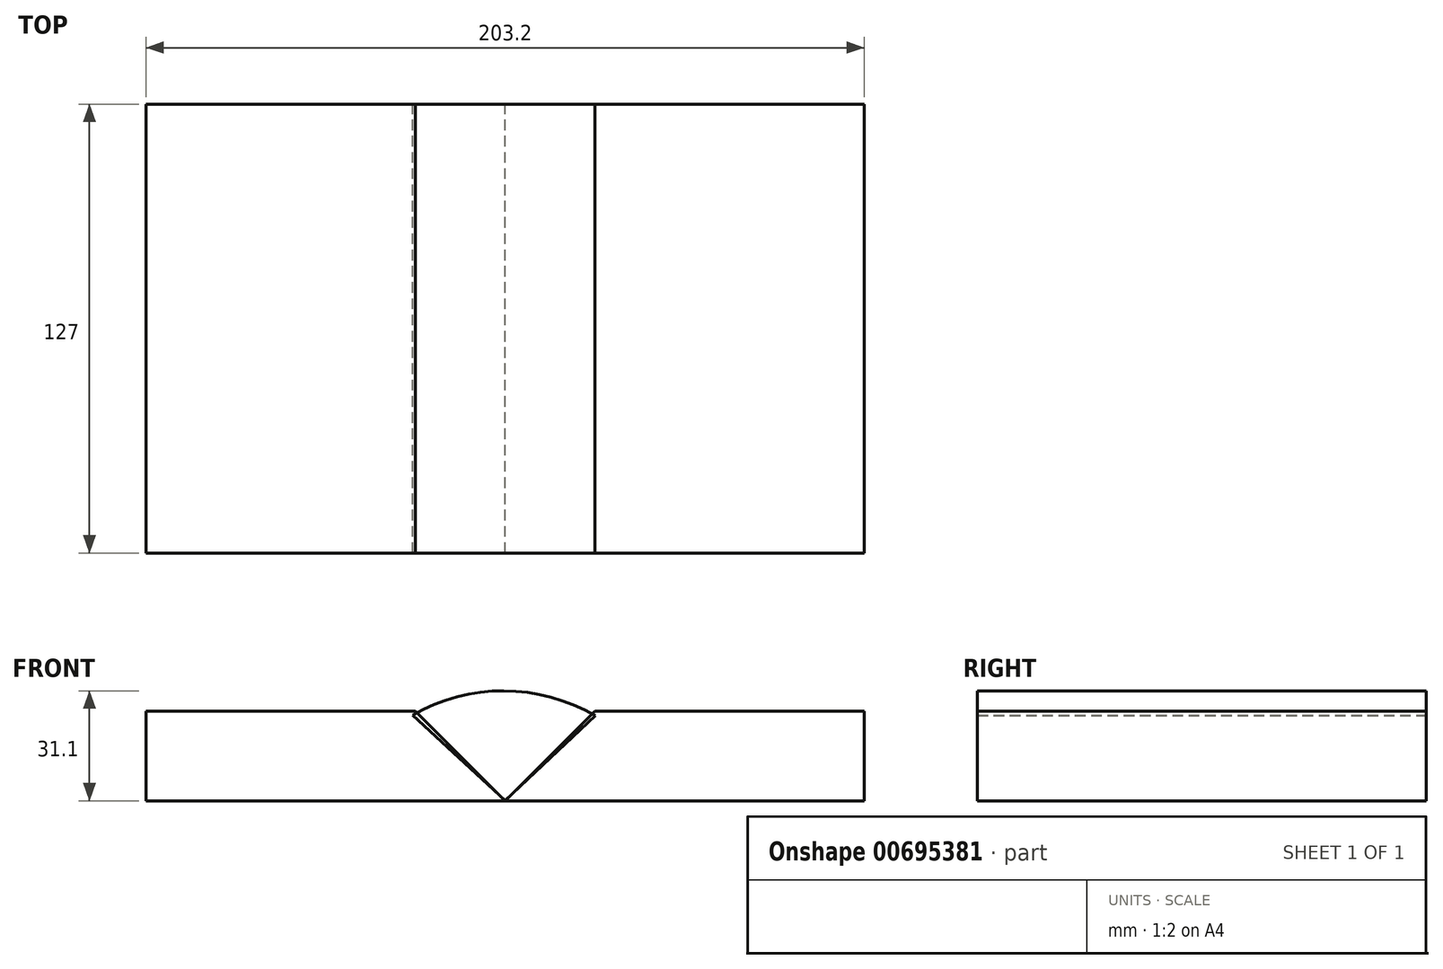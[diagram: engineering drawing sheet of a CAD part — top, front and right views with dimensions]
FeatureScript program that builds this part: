
annotation { "Feature Type Name" : "Feature", "Feature Type Description" : "" }
export const myFeature = defineFeature(function(context is Context, id is Id, definition is map)
    precondition{}
    {
        {
            var Q0;
            Q0=qCreatedBy(makeId("Front.planeOp"),FACE);
            var sketch = newSketch(context, id + "F0", { "sketchPlane" : qUnion([Q0])});
            skLineSegment(sketch, "E0.bottom", {"start": v(101.6, -12.7) * mm, "end": v(-101.6, -12.7) * mm});
            skLineSegment(sketch, "E0.top", {"start": v(101.6, 12.7) * mm, "end": v(25.4, 12.7) * mm});
            skLineSegment(sketch, "E0.left", {"start": v(101.6, -12.7) * mm, "end": v(101.6, 12.7) * mm});
            skLineSegment(sketch, "E0.right", {"start": v(-101.6, -12.7) * mm, "end": v(-101.6, 12.7) * mm});
            skPoint(sketch, "E0.middle", {"position": v(0, 0) * mm});
            skLineSegment(sketch, "E1", {"start": v(0, -12.7) * mm, "end": v(25.4, 12.7) * mm});
            skLineSegment(sketch, "E2", {"start": v(0, -12.7) * mm, "end": v(-25.4, 12.7) * mm});
            skLineSegment(sketch, "E3.trimOffspring", {"start": v(-25.4, 12.7) * mm, "end": v(-101.6, 12.7) * mm});
            skSolve(sketch);
        }
        {
            var Q0;
            Q0 = qSketchRegion(id + "F0", true);
            extrude(context, id + "F1", {"entities" : qUnion([Q0]), "endBound" : BoundingType.SYMMETRIC, "depth" : 127 * mm, "offsetDistance" : 25.4 * mm});
        }
        {
            var Q0;
            Q0=qCreatedBy(makeId("Front.planeOp"),FACE);
            var sketch = newSketch(context, id + "F2", { "sketchPlane" : qUnion([Q0])});
            skArc(sketch, "E4", {"start": v(25.47, 11.34) * mm, "mid": v(-0.34, 18.4) * mm, "end": v(-26.2, 11.54) * mm});
            skLineSegment(sketch, "E5", {"start": v(-26.2, 11.54) * mm, "end": v(0, -12.69) * mm});
            skLineSegment(sketch, "E6", {"start": v(0, -12.69) * mm, "end": v(25.47, 11.34) * mm});
            skSolve(sketch);
        }
        {
            var Q0;
            Q0 = qSketchRegion(id + "F2", true);
            extrude(context, id + "F3", {"entities" : qUnion([Q0]), "endBound" : BoundingType.SYMMETRIC, "depth" : 127 * mm, "offsetDistance" : 25.4 * mm});
        }
    });
